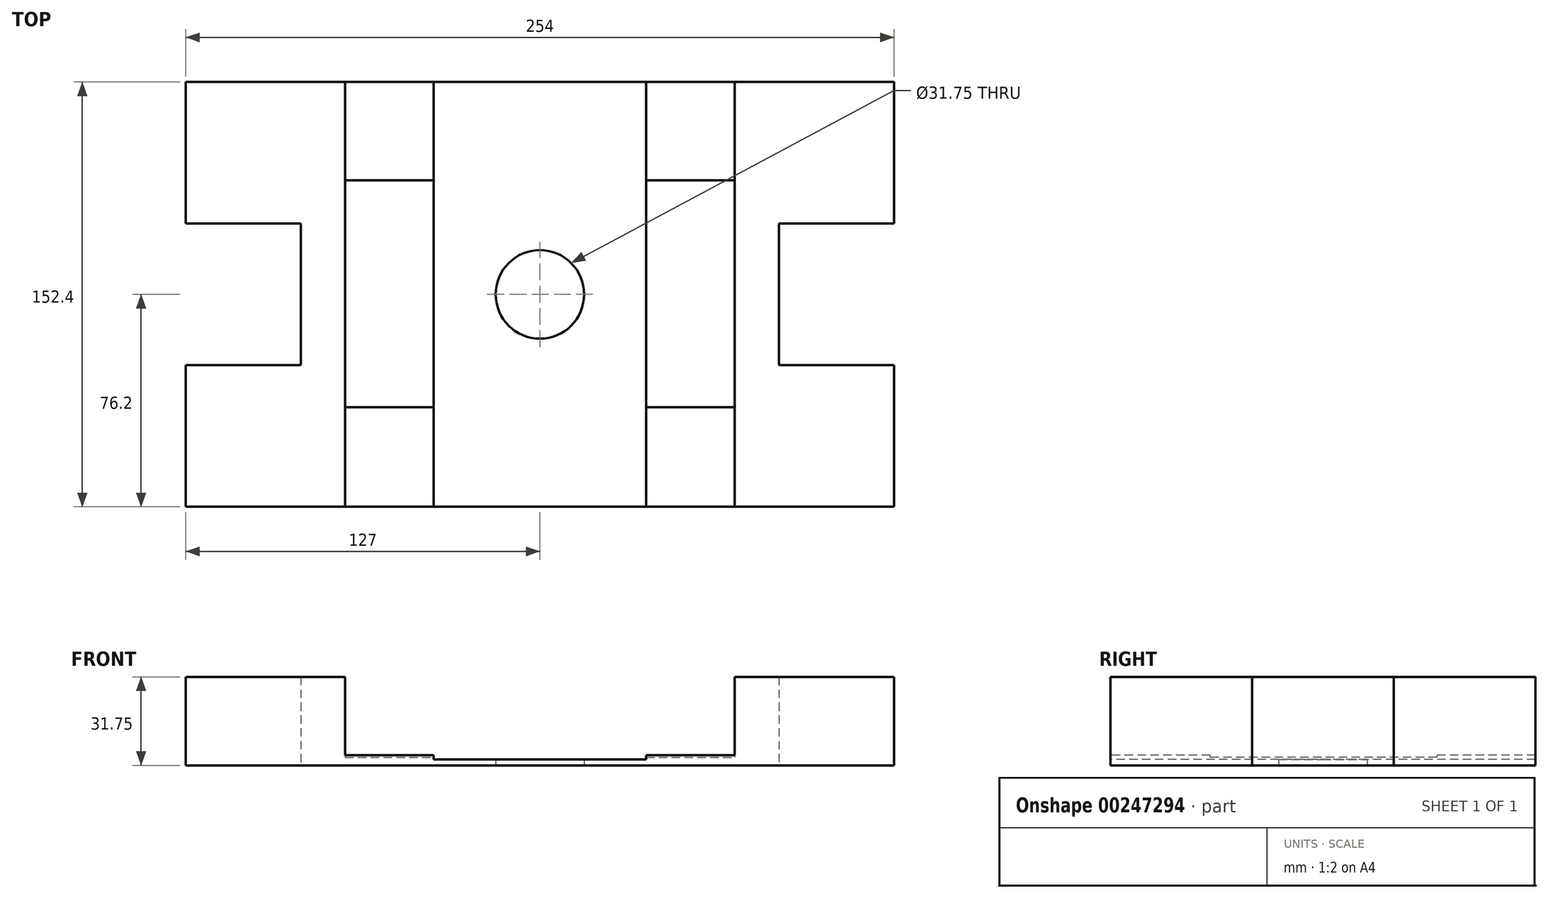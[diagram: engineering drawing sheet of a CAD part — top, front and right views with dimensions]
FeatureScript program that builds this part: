
annotation { "Feature Type Name" : "Feature", "Feature Type Description" : "" }
export const myFeature = defineFeature(function(context is Context, id is Id, definition is map)
    precondition{}
    {
        {
            var Q0;
            Q0=qCreatedBy(makeId("Top.planeOp"),FACE);
            var sketch = newSketch(context, id + "F0", { "sketchPlane" : qUnion([Q0])});
            skLineSegment(sketch, "E0.bottom", {"start": v(38.1, 76.2) * mm, "end": v(-38.1, 76.2) * mm});
            skLineSegment(sketch, "E0.top", {"start": v(38.1, -76.2) * mm, "end": v(-38.1, -76.2) * mm});
            skLineSegment(sketch, "E0.left", {"start": v(38.1, 76.2) * mm, "end": v(38.1, -76.2) * mm});
            skLineSegment(sketch, "E0.right", {"start": v(-38.1, 76.2) * mm, "end": v(-38.1, -76.2) * mm});
            skPoint(sketch, "E0.middle", {"position": v(0, 0) * mm});
            skCircle(sketch, "E1", {"center": v(0, 0) * mm, "radius": 15.88 * mm});
            skLineSegment(sketch, "E2.bottom", {"start": v(-38.1, 76.2) * mm, "end": v(-69.85, 76.2) * mm});
            skLineSegment(sketch, "E2.top", {"start": v(-38.1, -76.2) * mm, "end": v(-69.85, -76.2) * mm});
            skLineSegment(sketch, "E2.right", {"start": v(-69.85, 76.2) * mm, "end": v(-69.85, -76.2) * mm});
            skLineSegment(sketch, "E3.bottom", {"start": v(38.1, 76.2) * mm, "end": v(69.85, 76.2) * mm});
            skLineSegment(sketch, "E3.top", {"start": v(38.1, -76.2) * mm, "end": v(69.85, -76.2) * mm});
            skLineSegment(sketch, "E3.right", {"start": v(69.85, 76.2) * mm, "end": v(69.85, -76.2) * mm});
            skLineSegment(sketch, "E4.bottom", {"start": v(69.85, 76.2) * mm, "end": v(127, 76.2) * mm});
            skLineSegment(sketch, "E4.top", {"start": v(69.85, -76.2) * mm, "end": v(127, -76.2) * mm});
            skLineSegment(sketch, "E4.right", {"start": v(127, 76.2) * mm, "end": v(127, 25.4) * mm});
            skLineSegment(sketch, "E5.bottom", {"start": v(-69.85, 76.2) * mm, "end": v(-127, 76.2) * mm});
            skLineSegment(sketch, "E5.top", {"start": v(-69.85, -76.2) * mm, "end": v(-127, -76.2) * mm});
            skLineSegment(sketch, "E5.right", {"start": v(-127, 76.2) * mm, "end": v(-127, 25.4) * mm});
            skLineSegment(sketch, "E6", {"start": v(-127, 25.4) * mm, "end": v(-85.73, 25.4) * mm});
            skLineSegment(sketch, "E7", {"start": v(-69.85, 40.9) * mm, "end": v(-38.1, 40.9) * mm});
            skLineSegment(sketch, "E8", {"start": v(-127, -25.4) * mm, "end": v(-85.73, -25.4) * mm});
            skLineSegment(sketch, "E9", {"start": v(-69.85, -40.44) * mm, "end": v(-38.1, -40.44) * mm});
            skLineSegment(sketch, "E10.trimOffspring", {"start": v(85.73, 25.4) * mm, "end": v(127, 25.4) * mm});
            skLineSegment(sketch, "E11.trimOffspring", {"start": v(85.73, -25.4) * mm, "end": v(127, -25.4) * mm});
            skLineSegment(sketch, "E12.trimOffspring", {"start": v(38.1, -40.44) * mm, "end": v(69.85, -40.44) * mm});
            skLineSegment(sketch, "E13.trimOffspring", {"start": v(38.1, 40.9) * mm, "end": v(69.85, 40.9) * mm});
            skLineSegment(sketch, "E14", {"start": v(-85.73, 25.4) * mm, "end": v(-85.73, -25.4) * mm});
            skLineSegment(sketch, "E15", {"start": v(85.73, 25.4) * mm, "end": v(85.73, -25.4) * mm});
            skLineSegment(sketch, "E16.trimOffspring", {"start": v(-127, -25.4) * mm, "end": v(-127, -76.2) * mm});
            skLineSegment(sketch, "E17.trimOffspring", {"start": v(127, -25.4) * mm, "end": v(127, -76.2) * mm});
            skSolve(sketch);
        }
        {
            var Q0;
            {var subQ4=sQuery(id+"F0.wireOp",EDGE,"E5.bottom");Q0=makeQuery(id+"F0.imprint","IMPRINT",FACE,{"disambiguationData":[TD([[makeQuery(id+"F0.imprint","IMPRINT",EDGE,{"derivedFrom":subQ4}),1.0]])]});}
            var Q1;
            {var subQ3=sQuery(id+"F0.wireOp",EDGE,"E4.bottom");Q1=makeQuery(id+"F0.imprint","IMPRINT",FACE,{"disambiguationData":[TD([[makeQuery(id+"F0.imprint","IMPRINT",EDGE,{"derivedFrom":subQ3}),-1.0]])]});}
            extrude(context, id + "F1", {"entities" : qUnion([Q0, Q1]), "depth" : 31.75 * mm});
        }
        {
            var Q0;
            {var subQ0=sQuery(id+"F0.wireOp",EDGE,"E2.bottom");Q0=makeQuery(id+"F0.imprint","IMPRINT",FACE,{"disambiguationData":[TD([[makeQuery(id+"F0.imprint","IMPRINT",EDGE,{"derivedFrom":subQ0}),1.0]])]});}
            var Q1;
            {var subQ0=sQuery(id+"F0.wireOp",EDGE,"E2.top");Q1=makeQuery(id+"F0.imprint","IMPRINT",FACE,{"disambiguationData":[TD([[makeQuery(id+"F0.imprint","IMPRINT",EDGE,{"derivedFrom":subQ0}),-1.0]])]});}
            var Q2;
            {var subQ0=sQuery(id+"F0.wireOp",EDGE,"E3.bottom");Q2=makeQuery(id+"F0.imprint","IMPRINT",FACE,{"disambiguationData":[TD([[makeQuery(id+"F0.imprint","IMPRINT",EDGE,{"derivedFrom":subQ0}),-1.0]])]});}
            var Q3;
            {var subQ0=sQuery(id+"F0.wireOp",EDGE,"E3.top");Q3=makeQuery(id+"F0.imprint","IMPRINT",FACE,{"disambiguationData":[TD([[makeQuery(id+"F0.imprint","IMPRINT",EDGE,{"derivedFrom":subQ0}),1.0]])]});}
            extrude(context, id + "F2", {"entities" : qUnion([Q0, Q1, Q2, Q3]), "operationType" : NewBodyOperationType.ADD, "depth" : (3 + (5 / 8)) * mm});
        }
        {
            var Q0;
            {var subQ1=sQuery(id+"F0.wireOp",EDGE,"E0.bottom");Q0=makeQuery(id+"F0.imprint","IMPRINT",FACE,{"disambiguationData":[TD([[makeQuery(id+"F0.imprint","IMPRINT",EDGE,{"derivedFrom":subQ1}),1.0]])]});}
            extrude(context, id + "F3", {"entities" : qUnion([Q0]), "operationType" : NewBodyOperationType.ADD, "depth" : (3 + (5 / 8) - 1.5) * mm});
        }
        {
            var Q0;
            {var subQ0=sQuery(id+"F0.wireOp",EDGE,"E7");Q0=makeQuery(id+"F0.imprint","IMPRINT",FACE,{"disambiguationData":[TD([[makeQuery(id+"F0.imprint","IMPRINT",EDGE,{"derivedFrom":subQ0}),-1.0]])]});}
            var Q1;
            {var subQ0=sQuery(id+"F0.wireOp",EDGE,"E12.trimOffspring");Q1=makeQuery(id+"F0.imprint","IMPRINT",FACE,{"disambiguationData":[TD([[makeQuery(id+"F0.imprint","IMPRINT",EDGE,{"derivedFrom":subQ0}),1.0]])]});}
            extrude(context, id + "F4", {"entities" : qUnion([Q0, Q1]), "operationType" : NewBodyOperationType.ADD, "depth" : (3 + (5 / 8) - (3 / 4)) * mm});
        }
    });
